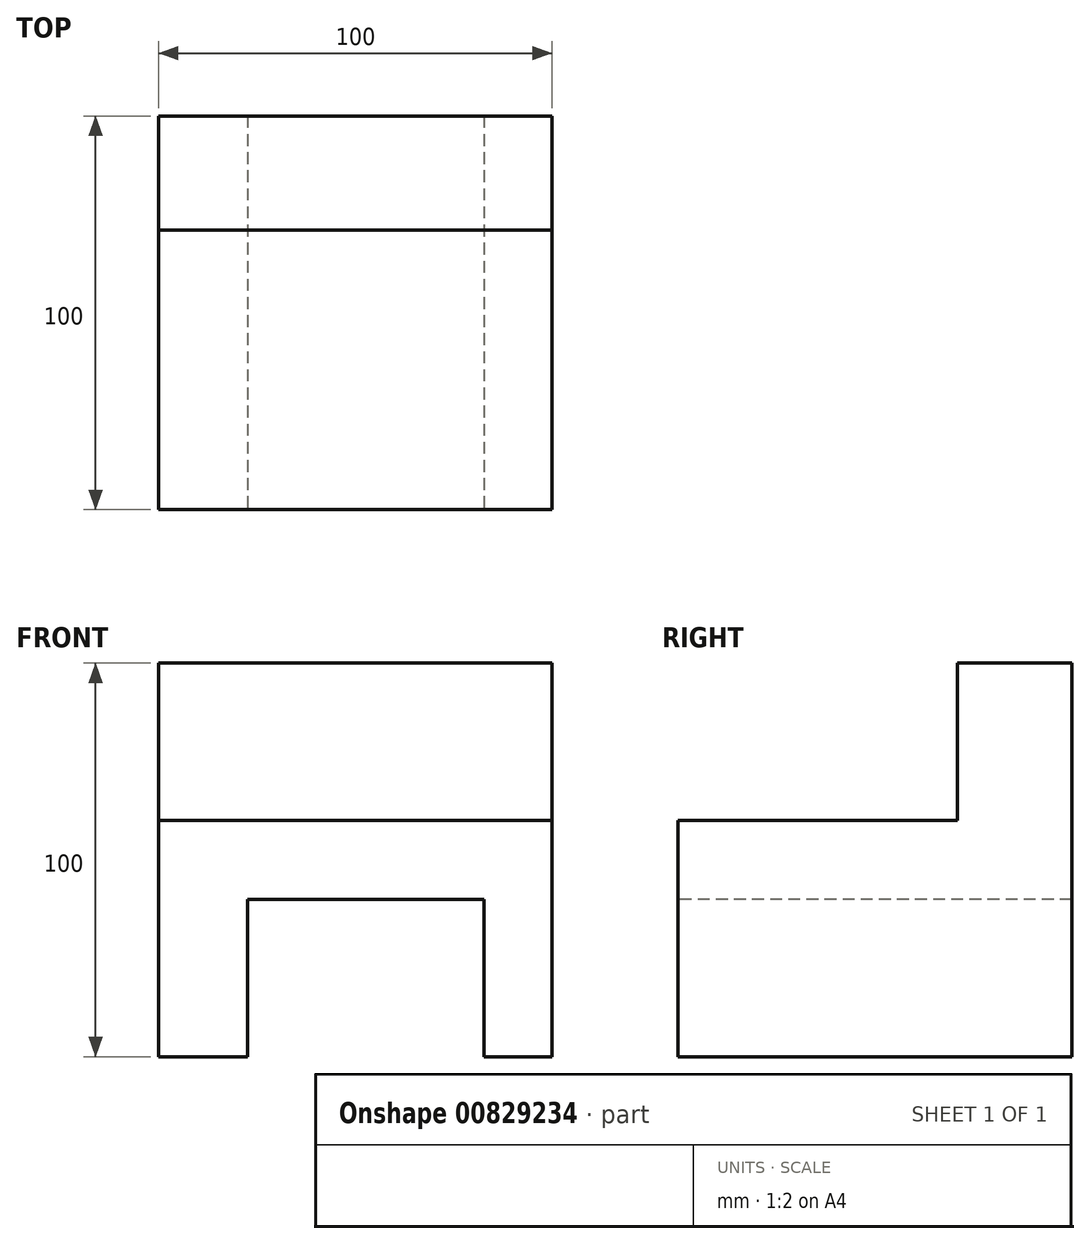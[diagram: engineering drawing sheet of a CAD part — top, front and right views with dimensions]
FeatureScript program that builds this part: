
annotation { "Feature Type Name" : "Feature", "Feature Type Description" : "" }
export const myFeature = defineFeature(function(context is Context, id is Id, definition is map)
    precondition{}
    {
        {
            var Q0;
            Q0=qCreatedBy(makeId("Top.planeOp"),FACE);
            var sketch = newSketch(context, id + "F0", { "sketchPlane" : qUnion([Q0])});
            skLineSegment(sketch, "E0.bottom", {"start": v(-50, 50) * mm, "end": v(50, 50) * mm});
            skLineSegment(sketch, "E0.top", {"start": v(-50, -50) * mm, "end": v(50, -50) * mm});
            skLineSegment(sketch, "E0.left", {"start": v(-50, 50) * mm, "end": v(-50, -50) * mm});
            skLineSegment(sketch, "E0.right", {"start": v(50, 50) * mm, "end": v(50, -50) * mm});
            skPoint(sketch, "E0.middle", {"position": v(0, 0) * mm});
            skSolve(sketch);
        }
        {
            var Q0;
            Q0 = qSketchRegion(id + "F0", true);
            extrude(context, id + "F1", {"entities" : qUnion([Q0]), "depth" : 100 * mm, "offsetDistance" : 25 * mm});
        }
        {
            var Q0;
            Q0=makeQuery(id+"F1.opExtrude","CAP_FACE",FACE,{"disambiguationData":[OSD([sQuery(id+"F0.wireOp",EDGE,"E0.bottom"),sQuery(id+"F0.wireOp",EDGE,"E0.top"),sQuery(id+"F0.wireOp",EDGE,"E0.left"),sQuery(id+"F0.wireOp",EDGE,"E0.right")])],"isStart":false});
            var sketch = newSketch(context, id + "F2", { "sketchPlane" : qUnion([Q0])});
            skLineSegment(sketch, "E1.bottom", {"start": v(-50, -50) * mm, "end": v(50, -50) * mm});
            skLineSegment(sketch, "E1.top", {"start": v(-50, 20.98) * mm, "end": v(50, 20.98) * mm});
            skLineSegment(sketch, "E1.left", {"start": v(-50, -50) * mm, "end": v(-50, 20.98) * mm});
            skLineSegment(sketch, "E1.right", {"start": v(50, -50) * mm, "end": v(50, 20.98) * mm});
            skSolve(sketch);
        }
        {
            var Q0;
            Q0 = qSketchRegion(id + "F2", true);
            extrude(context, id + "F3", {"entities" : qUnion([Q0]), "operationType" : NewBodyOperationType.REMOVE, "oppositeDirection" : true, "depth" : 40 * mm, "offsetDistance" : 25 * mm});
        }
        {
            var Q0;
            Q0=makeQuery(id+"F1.opExtrude","SWEPT_FACE",FACE,{"disambiguationData":[OSD([sQuery(id+"F0.wireOp",EDGE,"E0.top")])]});
            var sketch = newSketch(context, id + "F4", { "sketchPlane" : qUnion([Q0])});
            skLineSegment(sketch, "E2.bottom", {"start": v(-27.36, 40) * mm, "end": v(32.64, 40) * mm});
            skLineSegment(sketch, "E2.top", {"start": v(-27.36, 0) * mm, "end": v(32.64, 0) * mm});
            skLineSegment(sketch, "E2.left", {"start": v(-27.36, 40) * mm, "end": v(-27.36, 0) * mm});
            skLineSegment(sketch, "E2.right", {"start": v(32.64, 40) * mm, "end": v(32.64, 0) * mm});
            skSolve(sketch);
        }
        {
            var Q0;
            Q0 = qSketchRegion(id + "F4", true);
            extrude(context, id + "F5", {"entities" : qUnion([Q0]), "operationType" : NewBodyOperationType.REMOVE, "oppositeDirection" : true, "depth" : 100 * mm, "offsetDistance" : 25 * mm});
        }
    });
